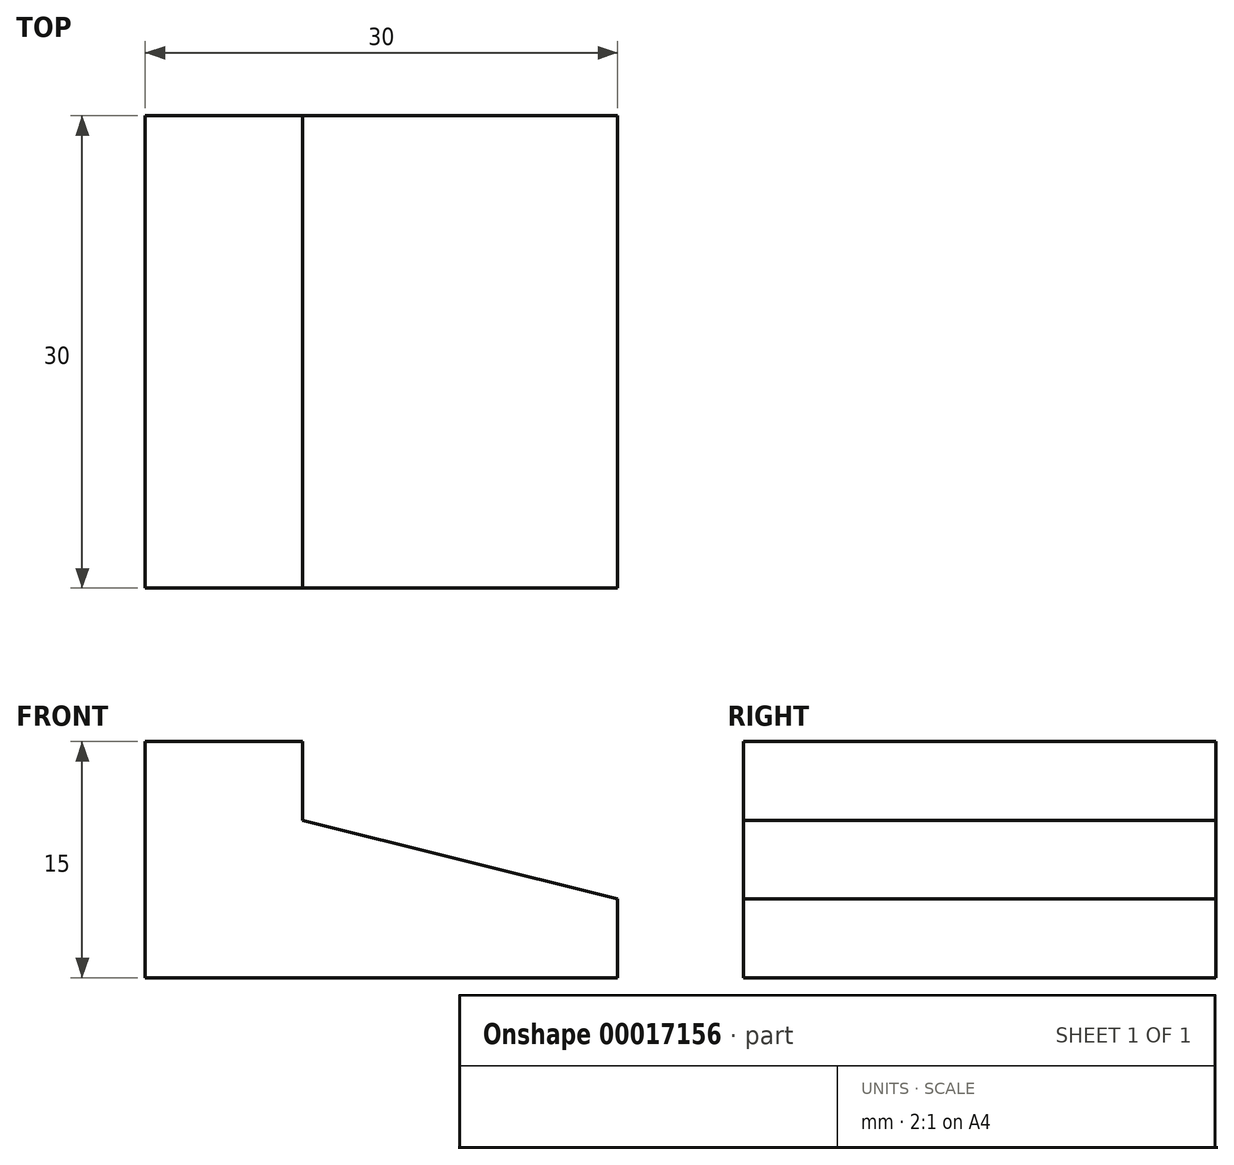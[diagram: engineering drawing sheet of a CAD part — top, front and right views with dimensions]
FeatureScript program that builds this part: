
annotation { "Feature Type Name" : "Feature", "Feature Type Description" : "" }
export const myFeature = defineFeature(function(context is Context, id is Id, definition is map)
    precondition{}
    {
        {
            var Q0;
            Q0=qCreatedBy(makeId("Front.planeOp"),FACE);
            var sketch = newSketch(context, id + "F0", { "sketchPlane" : qUnion([Q0])});
            skLineSegment(sketch, "E0", {"start": v(-22.8, 29.83) * mm, "end": v(-22.8, 14.83) * mm});
            skLineSegment(sketch, "E1", {"start": v(-22.8, 14.83) * mm, "end": v(7.2, 14.83) * mm});
            skLineSegment(sketch, "E2", {"start": v(7.2, 14.83) * mm, "end": v(7.2, 19.83) * mm});
            skLineSegment(sketch, "E3", {"start": v(7.2, 19.83) * mm, "end": v(-12.8, 24.83) * mm});
            skLineSegment(sketch, "E4", {"start": v(-12.8, 24.83) * mm, "end": v(-12.8, 29.83) * mm});
            skLineSegment(sketch, "E5", {"start": v(-22.8, 29.83) * mm, "end": v(-12.8, 29.83) * mm});
            skSolve(sketch);
        }
        {
            var Q0;
            Q0 = qSketchRegion(id + "F0", true);
            extrude(context, id + "F1", {"entities" : qUnion([Q0]), "depth" : 30 * mm});
        }
    });
